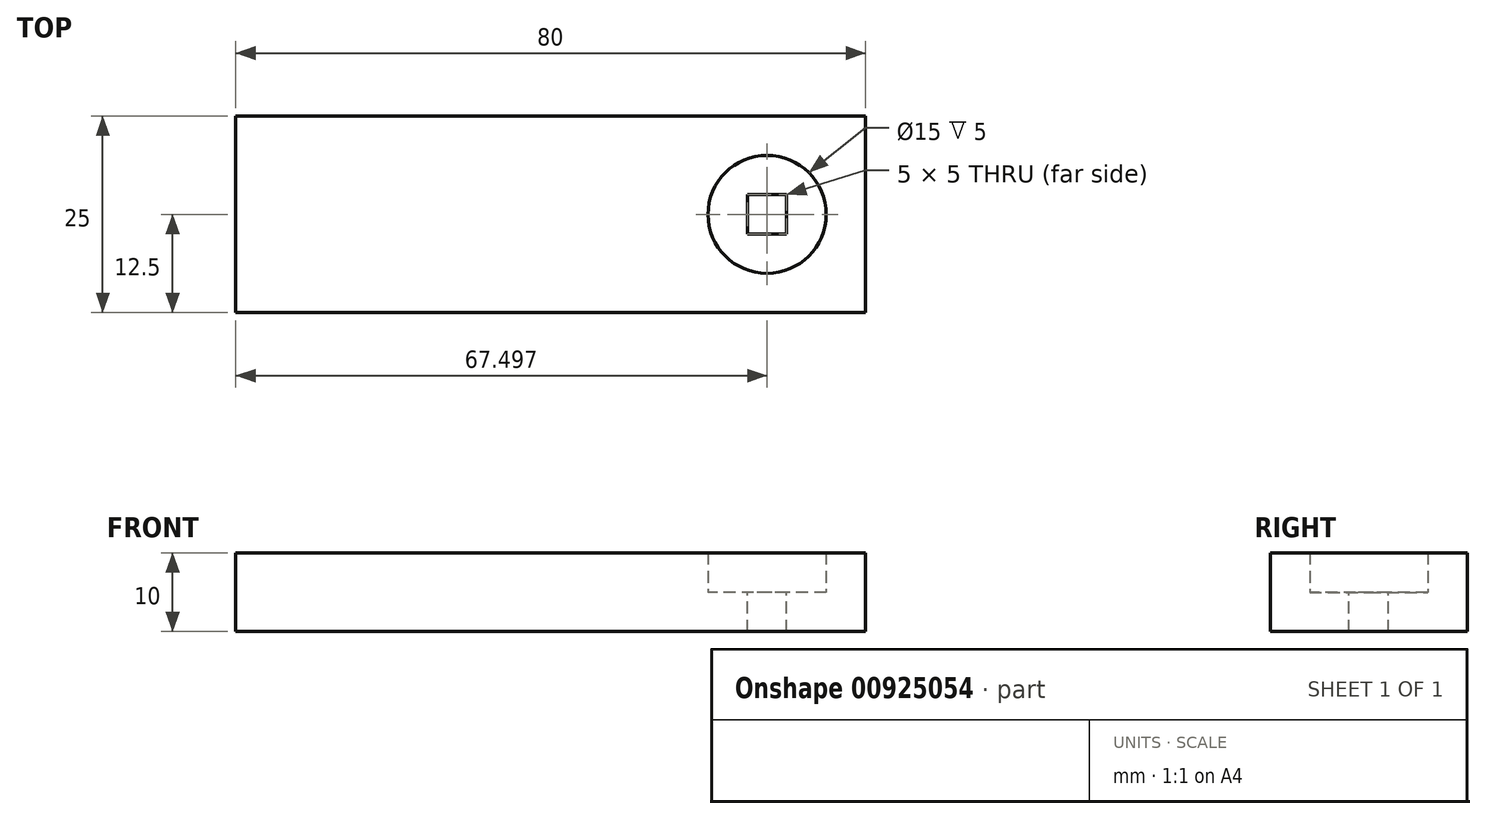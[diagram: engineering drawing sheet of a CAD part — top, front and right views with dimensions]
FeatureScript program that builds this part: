
annotation { "Feature Type Name" : "Feature", "Feature Type Description" : "" }
export const myFeature = defineFeature(function(context is Context, id is Id, definition is map)
    precondition{}
    {
        {
            var Q0;
            Q0=qCreatedBy(makeId("Top.planeOp"),FACE);
            var sketch = newSketch(context, id + "F0", { "sketchPlane" : qUnion([Q0])});
            skLineSegment(sketch, "E0.bottom", {"start": v(-89, 0) * mm, "end": v(-9, 0) * mm});
            skLineSegment(sketch, "E0.top", {"start": v(-89, 25) * mm, "end": v(-9, 25) * mm});
            skLineSegment(sketch, "E0.left", {"start": v(-89, 0) * mm, "end": v(-89, 25) * mm});
            skLineSegment(sketch, "E0.right", {"start": v(-9, 0) * mm, "end": v(-9, 25) * mm});
            skCircle(sketch, "E1", {"center": v(-21.5, 12.5) * mm, "radius": 7.5 * mm});
            skSolve(sketch);
        }
        {
            var Q0;
            Q0=makeQuery(id+"F0.imprint","IMPRINT",FACE,{"disambiguationData":[TD([[makeQuery(id+"F0.imprint","IMPRINT",EDGE,{"derivedFrom":sQuery(id+"F0.wireOp",EDGE,"E0.bottom")}),1.0]])]});
            extrude(context, id + "F1", {"entities" : qUnion([Q0]), "depth" : 5 * mm, "offsetDistance" : 25 * mm});
        }
        {
            var Q0;
            Q0=makeQuery(id+"F1.opExtrude","CAP_FACE",FACE,{"disambiguationData":[OSD([sQuery(id+"F0.wireOp",EDGE,"E0.bottom"),sQuery(id+"F0.wireOp",EDGE,"E0.top"),sQuery(id+"F0.wireOp",EDGE,"E0.left"),sQuery(id+"F0.wireOp",EDGE,"E0.right"),sQuery(id+"F0.wireOp",EDGE,"E1")])],"isStart":true});
            var sketch = newSketch(context, id + "F2", { "sketchPlane" : qUnion([Q0])});
            skLineSegment(sketch, "E2.bottom", {"start": v(-9, -25) * mm, "end": v(-89, -25) * mm});
            skLineSegment(sketch, "E2.top", {"start": v(-9, 0) * mm, "end": v(-89, 0) * mm});
            skLineSegment(sketch, "E2.left", {"start": v(-9, -25) * mm, "end": v(-9, 0) * mm});
            skLineSegment(sketch, "E2.right", {"start": v(-89, -25) * mm, "end": v(-89, 0) * mm});
            skLineSegment(sketch, "E3.bottom", {"start": v(-19, -15) * mm, "end": v(-24, -15) * mm});
            skLineSegment(sketch, "E3.top", {"start": v(-19, -10) * mm, "end": v(-24, -10) * mm});
            skLineSegment(sketch, "E3.left", {"start": v(-19, -15) * mm, "end": v(-19, -10) * mm});
            skLineSegment(sketch, "E3.right", {"start": v(-24, -15) * mm, "end": v(-24, -10) * mm});
            skSolve(sketch);
        }
        {
            var Q0;
            Q0=makeQuery(id+"F2.imprint","IMPRINT",FACE,{"disambiguationData":[TD([[makeQuery(id+"F2.imprint","IMPRINT",EDGE,{"derivedFrom":sQuery(id+"F2.wireOp",EDGE,"E3.bottom")}),1.0]])]});
            var Q1;
            Q1=makeQuery(id+"F2.imprint","IMPRINT",FACE,{"disambiguationData":[TD([[makeQuery(id+"F2.imprint","IMPRINT",EDGE,{"derivedFrom":sQuery(id+"F2.wireOp",EDGE,"E2.bottom")}),1.0]])]});
            extrude(context, id + "F3", {"entities" : qUnion([Q0, Q1]), "operationType" : NewBodyOperationType.ADD, "depth" : 5 * mm, "offsetDistance" : 25 * mm});
        }
    });
